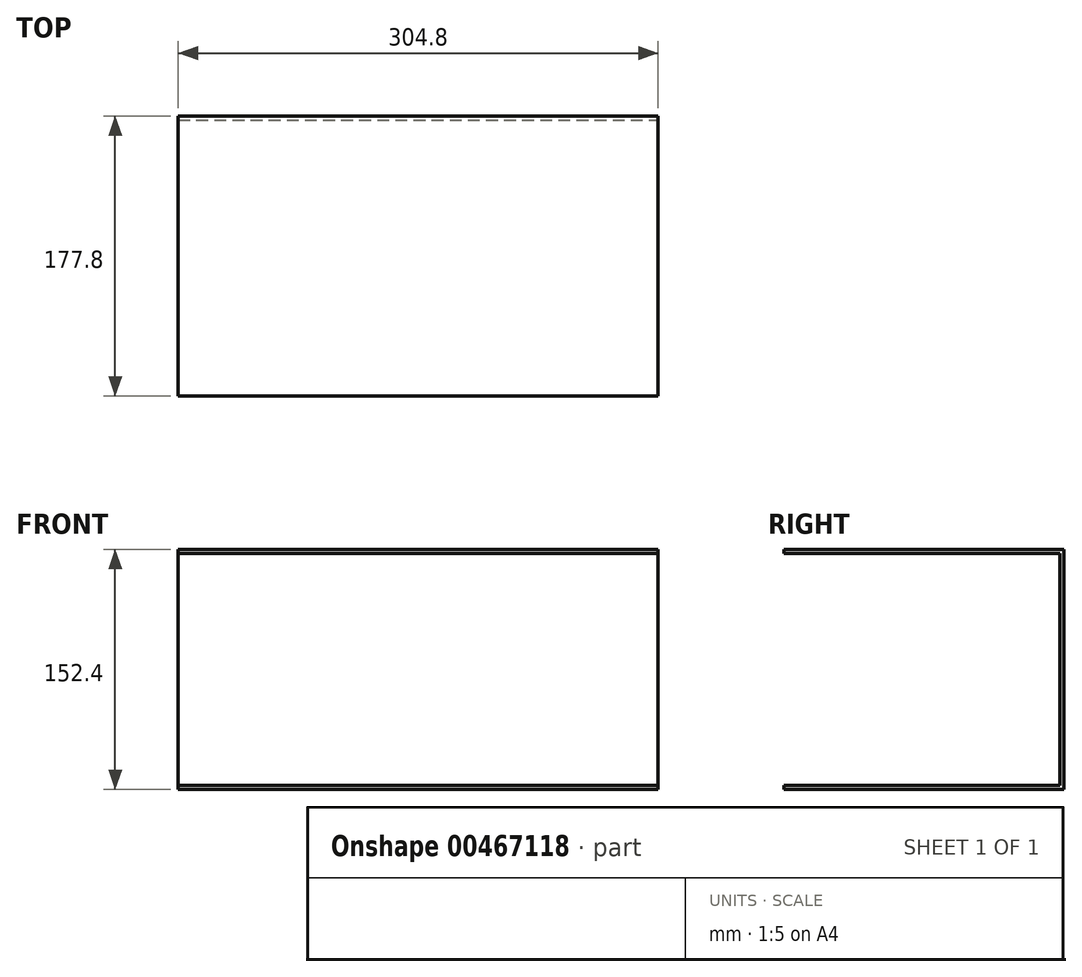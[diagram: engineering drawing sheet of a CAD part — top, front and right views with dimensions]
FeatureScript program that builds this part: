
annotation { "Feature Type Name" : "Feature", "Feature Type Description" : "" }
export const myFeature = defineFeature(function(context is Context, id is Id, definition is map)
    precondition{}
    {
        {
            var Q0;
            Q0=qCreatedBy(makeId("Front.planeOp"),FACE);
            var sketch = newSketch(context, id + "F0", { "sketchPlane" : qUnion([Q0])});
            skLineSegment(sketch, "E0.bottom", {"start": v(-196.11, 70.3) * mm, "end": v(108.69, 70.3) * mm});
            skLineSegment(sketch, "E0.top", {"start": v(-196.11, -82.1) * mm, "end": v(108.69, -82.1) * mm});
            skLineSegment(sketch, "E0.left", {"start": v(-196.11, 70.3) * mm, "end": v(-196.11, -82.1) * mm});
            skLineSegment(sketch, "E0.right", {"start": v(108.69, 70.3) * mm, "end": v(108.69, -82.1) * mm});
            skSolve(sketch);
        }
        {
            var Q0;
            Q0=makeQuery(id+"F0.imprint","IMPRINT",FACE,{"disambiguationData":[TD([[makeQuery(id+"F0.imprint","IMPRINT",EDGE,{"derivedFrom":sQuery(id+"F0.wireOp",EDGE,"E0.bottom")}),-1.0]])]});
            extrude(context, id + "F1", {"entities" : qUnion([Q0]), "endBound" : BoundingType.SYMMETRIC, "depth" : 177.8 * mm});
        }
        {
            var Q0;
            Q0=makeQuery(id+"F1.opExtrude","CAP_FACE",FACE,{"disambiguationData":[OSD([sQuery(id+"F0.wireOp",EDGE,"E0.bottom"),sQuery(id+"F0.wireOp",EDGE,"E0.top"),sQuery(id+"F0.wireOp",EDGE,"E0.left"),sQuery(id+"F0.wireOp",EDGE,"E0.right")])],"isStart":false});
            var Q1;
            Q1=makeQuery(id+"F1.opExtrude","SWEPT_FACE",FACE,{"disambiguationData":[OSD([sQuery(id+"F0.wireOp",EDGE,"E0.left")])]});
            var Q2;
            Q2=makeQuery(id+"F1.opExtrude","SWEPT_FACE",FACE,{"disambiguationData":[OSD([sQuery(id+"F0.wireOp",EDGE,"E0.right")])]});
            shell(context, id + "F2", {"entities" : qUnion([Q0, Q1, Q2]), "thickness" : 2.54 * mm});
        }
    });
